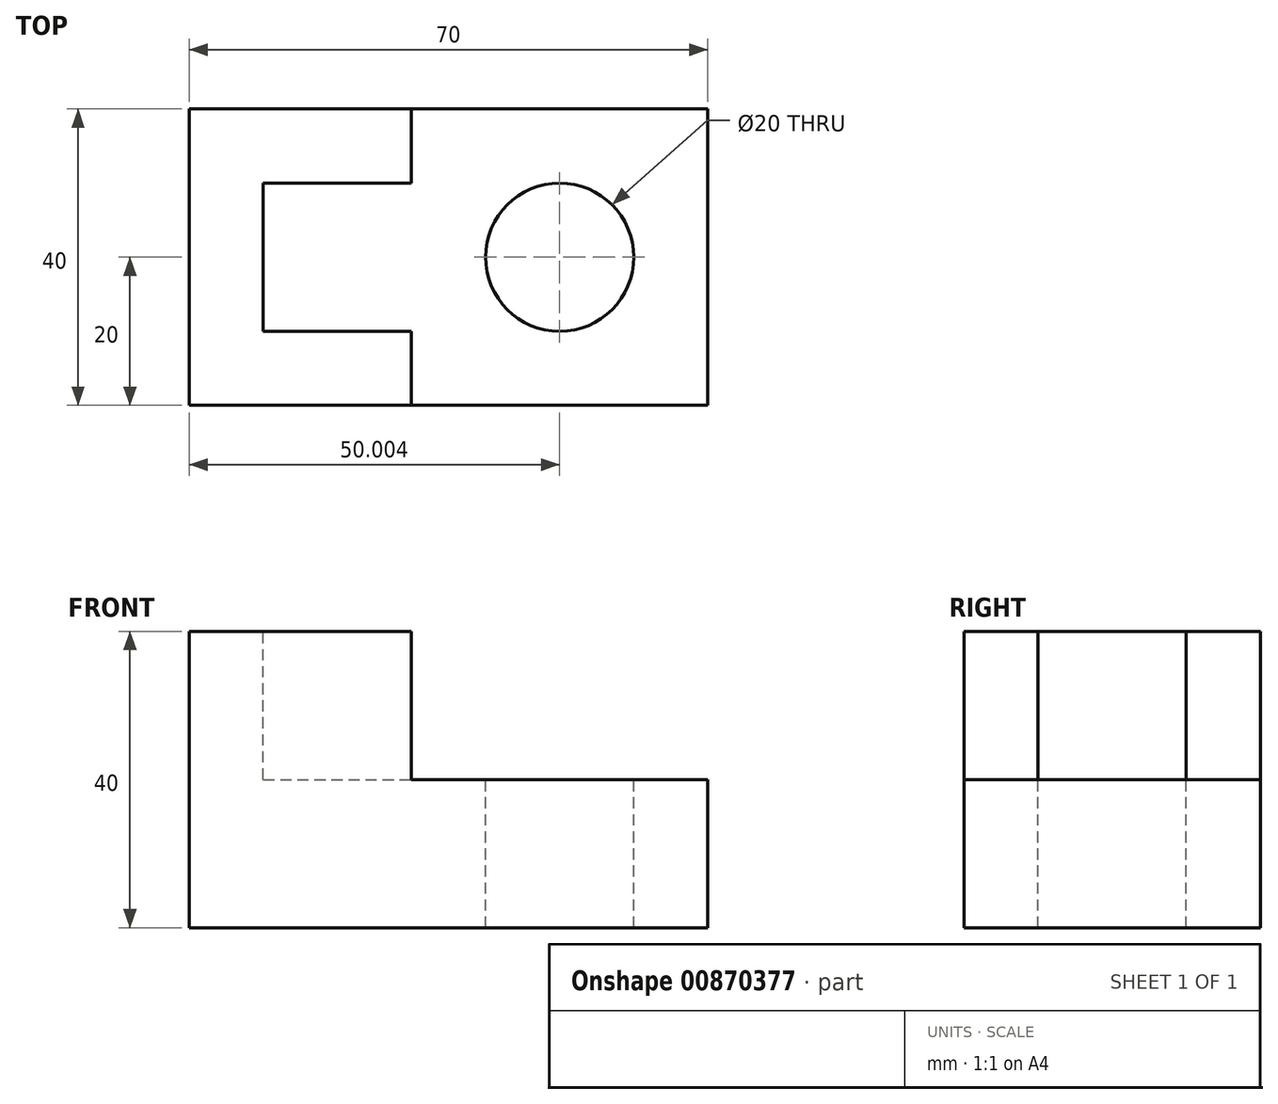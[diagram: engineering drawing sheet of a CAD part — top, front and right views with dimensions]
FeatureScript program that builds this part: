
annotation { "Feature Type Name" : "Feature", "Feature Type Description" : "" }
export const myFeature = defineFeature(function(context is Context, id is Id, definition is map)
    precondition{}
    {
        {
            var Q0;
            Q0=qCreatedBy(makeId("Front.planeOp"),FACE);
            var sketch = newSketch(context, id + "F0", { "sketchPlane" : qUnion([Q0])});
            skLineSegment(sketch, "E0.bottom", {"start": v(-36.59, 18.19) * mm, "end": v(-6.59, 18.19) * mm});
            skLineSegment(sketch, "E0.top", {"start": v(-36.59, -21.81) * mm, "end": v(33.41, -21.81) * mm});
            skLineSegment(sketch, "E0.left", {"start": v(-36.59, 18.19) * mm, "end": v(-36.59, -21.81) * mm});
            skLineSegment(sketch, "E0.right", {"start": v(33.41, -1.81) * mm, "end": v(33.41, -21.81) * mm});
            skLineSegment(sketch, "E1", {"start": v(-6.59, 18.19) * mm, "end": v(-6.59, -1.81) * mm});
            skLineSegment(sketch, "E2", {"start": v(-6.59, -1.81) * mm, "end": v(33.41, -1.81) * mm});
            skLineSegment(sketch, "E3", {"start": v(-26.59, 18.19) * mm, "end": v(-6.59, -1.81) * mm});
            skSolve(sketch);
        }
        {
            var Q0;
            Q0 = qSketchRegion(id + "F0", true);
            extrude(context, id + "F1", {"entities" : qUnion([Q0]), "depth" : 40 * mm, "offsetDistance" : 25 * mm});
        }
        {
            var Q0;
            Q0=makeQuery(id+"F1.opExtrude","SWEPT_FACE",FACE,{"disambiguationData":[OSD([sQuery(id+"F0.wireOp",EDGE,"E0.bottom")])]});
            var sketch = newSketch(context, id + "F2", { "sketchPlane" : qUnion([Q0])});
            skLineSegment(sketch, "E4.bottom", {"start": v(-36.59, 0) * mm, "end": v(-6.59, 0) * mm});
            skLineSegment(sketch, "E4.top", {"start": v(-36.59, -10) * mm, "end": v(-6.59, -10) * mm});
            skLineSegment(sketch, "E4.left", {"start": v(-36.59, 0) * mm, "end": v(-36.59, -10) * mm});
            skLineSegment(sketch, "E4.right", {"start": v(-6.59, 0) * mm, "end": v(-6.59, -10) * mm});
            skLineSegment(sketch, "E5.bottom", {"start": v(-36.59, -10) * mm, "end": v(-26.59, -10) * mm});
            skLineSegment(sketch, "E5.top", {"start": v(-36.59, -40) * mm, "end": v(-26.59, -40) * mm});
            skLineSegment(sketch, "E5.left", {"start": v(-36.59, -10) * mm, "end": v(-36.59, -40) * mm});
            skLineSegment(sketch, "E5.right", {"start": v(-26.59, -10) * mm, "end": v(-26.59, -40) * mm});
            skLineSegment(sketch, "E6", {"start": v(-6.59, -30) * mm, "end": v(-26.59, -30) * mm});
            skLineSegment(sketch, "E7", {"start": v(-6.59, -30) * mm, "end": v(-6.59, -40) * mm});
            skLineSegment(sketch, "E8", {"start": v(-6.59, -40) * mm, "end": v(-26.59, -40) * mm});
            skSolve(sketch);
        }
        {
            var Q0;
            {var subQ0=sQuery(id+"F2.wireOp",EDGE,"E4.top");Q0=makeQuery(id+"F2.imprint","IMPRINT",FACE,{"disambiguationData":[TD([[makeQuery(id+"F2.imprint","IMPRINT",EDGE,{"derivedFrom":subQ0}),-1.0]])]});}
            extrude(context, id + "F3", {"entities" : qUnion([Q0]), "operationType" : NewBodyOperationType.REMOVE, "oppositeDirection" : true, "depth" : 20 * mm, "offsetDistance" : 25 * mm});
        }
        {
            var Q0;
            Q0=makeQuery(id+"F3.boolean.opBoolean","MERGE",FACE,{"derivedFrom":[makeQuery(id+"F1.opExtrude","SWEPT_FACE",FACE,{"disambiguationData":[OSD([sQuery(id+"F0.wireOp",EDGE,"E2")])]}),makeQuery(id+"F3.opExtrude","CAP_FACE",FACE,{"disambiguationData":[OSD([sQuery(id+"F0.wireOp",EDGE,"E0.bottom"),sQuery(id+"F0.wireOp",EDGE,"E1"),sQuery(id+"F2.wireOp",EDGE,"E4.top"),sQuery(id+"F2.wireOp",EDGE,"E5.right"),sQuery(id+"F2.wireOp",EDGE,"E6")])],"isStart":false})]});
            var sketch = newSketch(context, id + "F4", { "sketchPlane" : qUnion([Q0])});
            skCircle(sketch, "E9", {"center": v(13.41, -20) * mm, "radius": 10 * mm});
            skSolve(sketch);
        }
        {
            var Q0;
            Q0=makeQuery(id+"F4.imprint","IMPRINT",FACE,{"disambiguationData":[TD([[makeQuery(id+"F4.imprint","IMPRINT",EDGE,{"derivedFrom":sQuery(id+"F4.wireOp",EDGE,"E9")}),1.0]])]});
            extrude(context, id + "F5", {"entities" : qUnion([Q0]), "operationType" : NewBodyOperationType.REMOVE, "oppositeDirection" : true, "depth" : 20 * mm, "offsetDistance" : 25 * mm});
        }
    });
